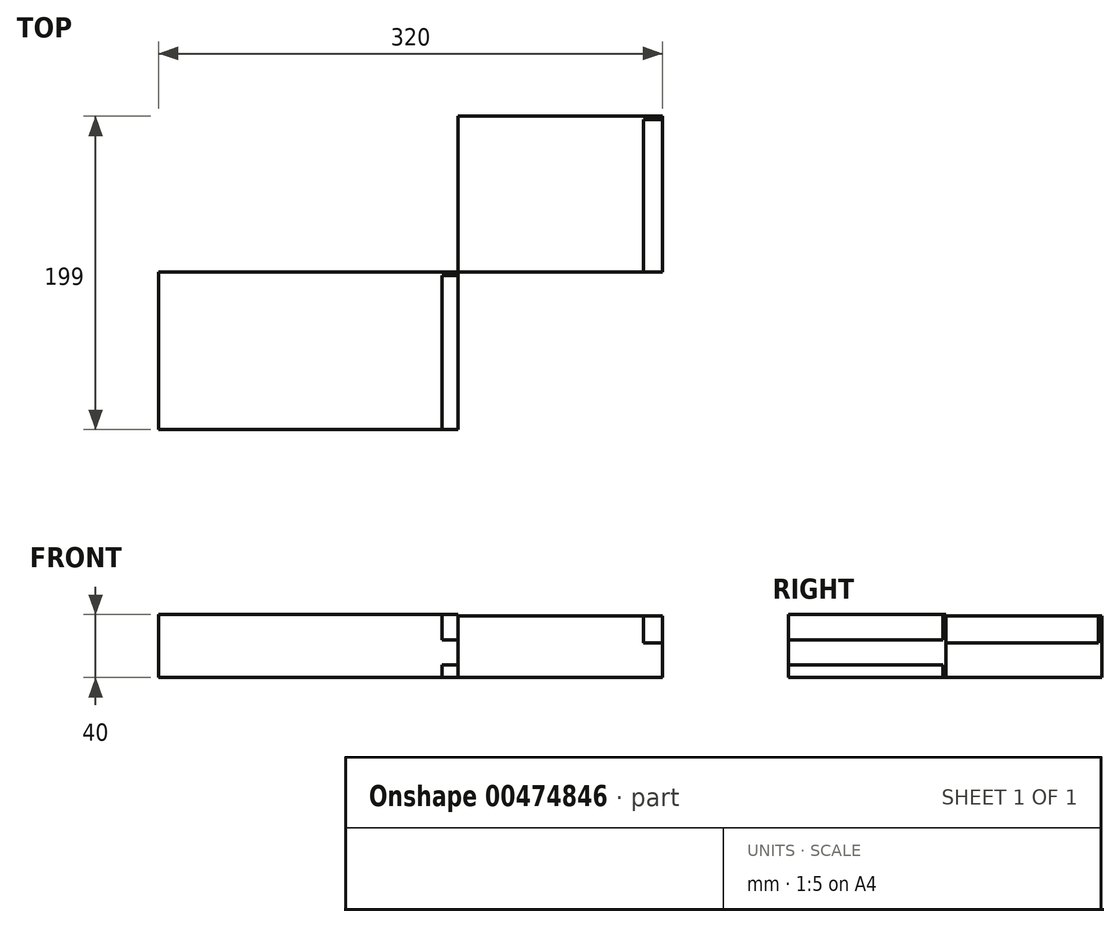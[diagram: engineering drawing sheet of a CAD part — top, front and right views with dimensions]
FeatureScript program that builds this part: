
annotation { "Feature Type Name" : "Feature", "Feature Type Description" : "" }
export const myFeature = defineFeature(function(context is Context, id is Id, definition is map)
    precondition{}
    {
        {
            var Q0;
            Q0=qCreatedBy(makeId("Top.planeOp"),FACE);
            var sketch = newSketch(context, id + "F0", { "sketchPlane" : qUnion([Q0])});
            skLineSegment(sketch, "E0.bottom", {"start": v(0, 0) * mm, "end": v(130, 0) * mm});
            skLineSegment(sketch, "E0.top", {"start": v(0, 99) * mm, "end": v(130, 99) * mm});
            skLineSegment(sketch, "E0.left", {"start": v(0, 0) * mm, "end": v(0, 99) * mm});
            skLineSegment(sketch, "E0.right", {"start": v(130, 0) * mm, "end": v(130, 99) * mm});
            skLineSegment(sketch, "E1", {"start": v(118, 99) * mm, "end": v(118, 0) * mm});
            skLineSegment(sketch, "E2.bottom", {"start": v(0, 0) * mm, "end": v(-190, 0) * mm});
            skLineSegment(sketch, "E2.top", {"start": v(0, -100) * mm, "end": v(-190, -100) * mm});
            skLineSegment(sketch, "E2.left", {"start": v(0, 0) * mm, "end": v(0, -100) * mm});
            skLineSegment(sketch, "E2.right", {"start": v(-190, 0) * mm, "end": v(-190, -100) * mm});
            skLineSegment(sketch, "E3", {"start": v(-10, -100) * mm, "end": v(-10, 0) * mm});
            skLineSegment(sketch, "E4", {"start": v(0, 97) * mm, "end": v(130, 97) * mm});
            skLineSegment(sketch, "E5", {"start": v(-190, -2) * mm, "end": v(0, -2) * mm});
            skSolve(sketch);
        }
        {
            var Q0;
            {var subQ0=sQuery(id+"F0.wireOp",EDGE,"E0.right");Q0=makeQuery(id+"F0.imprint","IMPRINT",FACE,{"disambiguationData":[TD([[makeQuery(id+"F0.imprint","IMPRINT",EDGE,{"derivedFrom":subQ0}),1.0]])]});}
            extrude(context, id + "F1", {"entities" : qUnion([Q0]), "depth" : 22 * mm});
        }
        {
            var Q0;
            {var subQ0=sQuery(id+"F0.wireOp",EDGE,"E0.left");Q0=makeQuery(id+"F0.imprint","IMPRINT",FACE,{"disambiguationData":[TD([[makeQuery(id+"F0.imprint","IMPRINT",EDGE,{"derivedFrom":subQ0}),-1.0]])]});}
            var Q1;
            {var subQ0=sQuery(id+"F0.wireOp",EDGE,"E0.right");var subQ1=sQuery(id+"F0.wireOp",EDGE,"E0.top");var subQ2=makeQuery(id+"F0.imprint","INTERSECT",VERTEX,{"derivedFrom":[subQ1,subQ0]});Q1=makeQuery(id+"F0.imprint","IMPRINT",FACE,{"disambiguationData":[TD([[makeQuery(id+"F0.imprint","IMPRINT",EDGE,{"disambiguationData":[TD([[subQ2,1.0]])],"derivedFrom":subQ1}),-1.0]])]});}
            extrude(context, id + "F2", {"entities" : qUnion([Q0, Q1]), "operationType" : NewBodyOperationType.ADD, "depth" : 39 * mm});
        }
        {
            var Q0;
            {var subQ0=sQuery(id+"F0.wireOp",EDGE,"E2.right");Q0=makeQuery(id+"F0.imprint","IMPRINT",FACE,{"disambiguationData":[TD([[makeQuery(id+"F0.imprint","IMPRINT",EDGE,{"derivedFrom":subQ0}),1.0]])]});}
            var Q1;
            {var subQ1=sQuery(id+"F0.wireOp",EDGE,"E2.bottom");var subQ3=sQuery(id+"F0.wireOp",EDGE,"E3");var subQ4=makeQuery(id+"F0.imprint","INTERSECT",VERTEX,{"derivedFrom":[subQ1,subQ3]});Q1=makeQuery(id+"F0.imprint","IMPRINT",FACE,{"disambiguationData":[TD([[makeQuery(id+"F0.imprint","IMPRINT",EDGE,{"disambiguationData":[TD([[subQ4,1.0]])],"derivedFrom":subQ3}),-1.0]])]});}
            extrude(context, id + "F3", {"entities" : qUnion([Q0, Q1]), "depth" : 40 * mm});
        }
        {
            var Q0;
            {var subQ0=sQuery(id+"F0.wireOp",EDGE,"E2.left");Q0=makeQuery(id+"F0.imprint","IMPRINT",FACE,{"disambiguationData":[TD([[makeQuery(id+"F0.imprint","IMPRINT",EDGE,{"derivedFrom":subQ0}),-1.0]])]});}
            extrude(context, id + "F4", {"entities" : qUnion([Q0]), "operationType" : NewBodyOperationType.ADD, "depth" : 24 * mm});
        }
        {
            var Q0;
            {var subQ0=sQuery(id+"F0.wireOp",EDGE,"E2.left");Q0=makeQuery(id+"F4.boolean.opBoolean","MERGE",FACE,{"derivedFrom":[makeQuery(id+"F3.opExtrude","SWEPT_FACE",FACE,{"disambiguationData":[OSD([subQ0])]}),makeQuery(id+"F4.opExtrude","SWEPT_FACE",FACE,{"disambiguationData":[OSD([subQ0])]})]});}
            var sketch = newSketch(context, id + "F5", { "sketchPlane" : qUnion([Q0])});
            skLineSegment(sketch, "E6.bottom", {"start": v(-100, 0) * mm, "end": v(-2, 0) * mm});
            skLineSegment(sketch, "E6.top", {"start": v(-100, 8) * mm, "end": v(-2, 8) * mm});
            skLineSegment(sketch, "E6.left", {"start": v(-100, 0) * mm, "end": v(-100, 8) * mm});
            skLineSegment(sketch, "E6.right", {"start": v(-2, 0) * mm, "end": v(-2, 8) * mm});
            skSolve(sketch);
        }
        {
            var Q0;
            Q0=makeQuery(id+"F5.imprint","IMPRINT",FACE,{"disambiguationData":[TD([[makeQuery(id+"F5.imprint","IMPRINT",EDGE,{"derivedFrom":sQuery(id+"F5.wireOp",EDGE,"E6.bottom")}),-1.0]])]});
            extrude(context, id + "F6", {"entities" : qUnion([Q0]), "operationType" : NewBodyOperationType.REMOVE, "oppositeDirection" : true, "depth" : 10 * mm});
        }
    });
